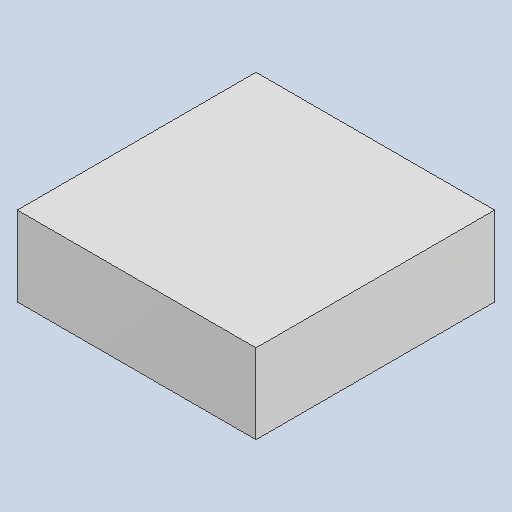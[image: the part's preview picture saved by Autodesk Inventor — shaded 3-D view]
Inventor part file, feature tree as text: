
AUTODESK INVENTOR PART (.ipt)
format: ipt  version: 2023.4 (Build 274418000, 418)  size: 79,872 bytes
history: native  units: mm
features: extrude x1
ambient origin geometry x8: Origin, YZ Plane, XZ Plane, XY Plane, X Axis, Y Axis, Z Axis, Center Point
bodies: Solid1 (feature_tree)
feature tree (1):
  extrude  "Extruded_3"  [1 undecoded]
note: 1 required parameter value undecoded (feature->parameter linkage not recoverable at this tier; creation-order binding heuristic only, values carry confidence <= 0.55)
